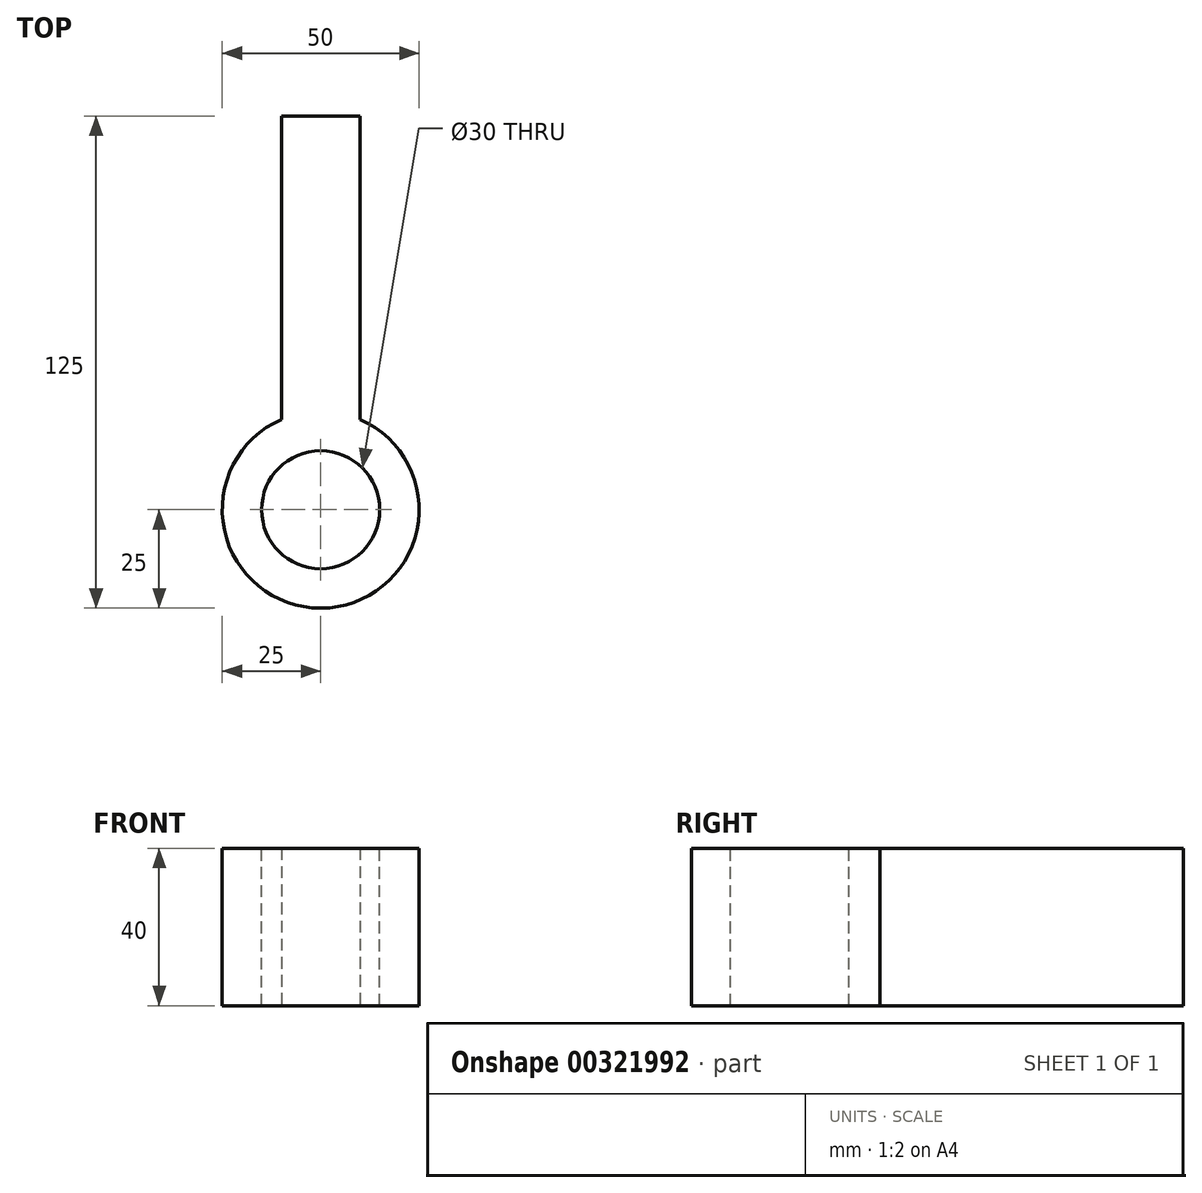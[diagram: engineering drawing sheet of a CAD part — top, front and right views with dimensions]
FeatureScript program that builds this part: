
annotation { "Feature Type Name" : "Feature", "Feature Type Description" : "" }
export const myFeature = defineFeature(function(context is Context, id is Id, definition is map)
    precondition{}
    {
        {
            var Q0;
            Q0=qCreatedBy(makeId("Top.planeOp"),FACE);
            var sketch = newSketch(context, id + "F0", { "sketchPlane" : qUnion([Q0])});
            skCircle(sketch, "E0", {"center": v(0, 0) * mm, "radius": 25 * mm});
            skSolve(sketch);
        }
        {
            var Q0;
            Q0 = qSketchRegion(id + "F0", true);
            extrude(context, id + "F1", {"entities" : qUnion([Q0]), "depth" : 40 * mm});
        }
        {
            var Q0;
            Q0=qCreatedBy(makeId("Front.planeOp"),FACE);
            var sketch = newSketch(context, id + "F2", { "sketchPlane" : qUnion([Q0])});
            skLineSegment(sketch, "E1.bottom", {"start": v(-10, 40) * mm, "end": v(10, 40) * mm});
            skPoint(sketch, "E1.middle", {"position": v(0, 0) * mm});
            skLineSegment(sketch, "E2", {"start": v(10, 0) * mm, "end": v(-10, 0) * mm});
            skLineSegment(sketch, "E3", {"start": v(10, 40) * mm, "end": v(10, 0) * mm});
            skLineSegment(sketch, "E4", {"start": v(-10, 0) * mm, "end": v(-10, 40) * mm});
            skSolve(sketch);
        }
        {
            var Q0;
            Q0 = qSketchRegion(id + "F2", true);
            extrude(context, id + "F3", {"entities" : qUnion([Q0]), "operationType" : NewBodyOperationType.ADD, "oppositeDirection" : true, "depth" : 100 * mm});
        }
        {
            var Q0;
            Q0=makeQuery(id+"F1.opExtrude","CAP_FACE",FACE,{"disambiguationData":[OSD([sQuery(id+"F0.wireOp",EDGE,"E0")])],"isStart":false});
            var sketch = newSketch(context, id + "F4", { "sketchPlane" : qUnion([Q0])});
            skCircle(sketch, "E5", {"center": v(0, 0) * mm, "radius": 15 * mm});
            skSolve(sketch);
        }
        {
            var Q0;
            Q0 = qSketchRegion(id + "F4", true);
            extrude(context, id + "F5", {"entities" : qUnion([Q0]), "operationType" : NewBodyOperationType.REMOVE, "oppositeDirection" : true, "depth" : 43 * mm});
        }
    });
